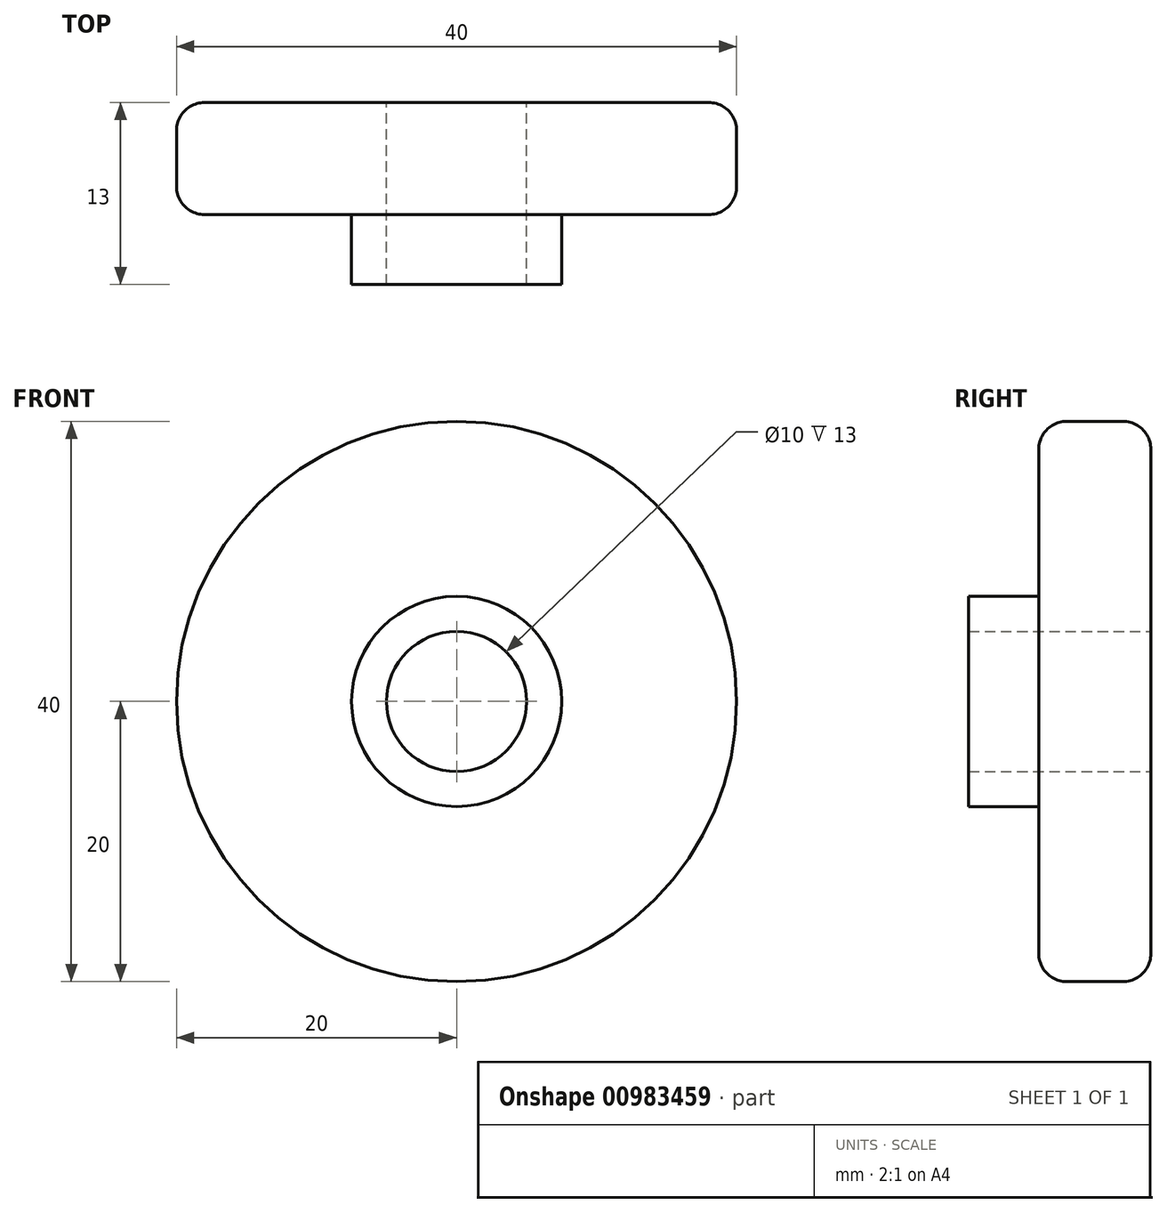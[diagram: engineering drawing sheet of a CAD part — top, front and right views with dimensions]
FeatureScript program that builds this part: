
annotation { "Feature Type Name" : "Feature", "Feature Type Description" : "" }
export const myFeature = defineFeature(function(context is Context, id is Id, definition is map)
    precondition{}
    {
        {
            var Q0;
            Q0=qCreatedBy(makeId("Front.planeOp"),FACE);
            var sketch = newSketch(context, id + "F0", { "sketchPlane" : qUnion([Q0])});
            skCircle(sketch, "E0", {"center": v(0, 0) * mm, "radius": 5 * mm});
            skCircle(sketch, "E1", {"center": v(0, 0) * mm, "radius": 20 * mm});
            skCircle(sketch, "E2", {"center": v(0, 0) * mm, "radius": 7.5 * mm});
            skSolve(sketch);
        }
        {
            var Q0;
            Q0=makeQuery(id+"F0.imprint","IMPRINT",FACE,{"disambiguationData":[TD([[makeQuery(id+"F0.imprint","IMPRINT",EDGE,{"derivedFrom":sQuery(id+"F0.wireOp",EDGE,"E1")}),1.0]])]});
            var Q1;
            Q1=makeQuery(id+"F0.imprint","IMPRINT",FACE,{"disambiguationData":[TD([[makeQuery(id+"F0.imprint","IMPRINT",EDGE,{"derivedFrom":sQuery(id+"F0.wireOp",EDGE,"E0")}),-1.0]])]});
            extrude(context, id + "F1", {"entities" : qUnion([Q0, Q1]), "depth" : 8 * mm, "offsetDistance" : 25 * mm});
        }
        {
            var Q0;
            Q0=makeQuery(id+"F0.imprint","IMPRINT",FACE,{"disambiguationData":[TD([[makeQuery(id+"F0.imprint","IMPRINT",EDGE,{"derivedFrom":sQuery(id+"F0.wireOp",EDGE,"E0")}),-1.0]])]});
            extrude(context, id + "F2", {"entities" : qUnion([Q0]), "operationType" : NewBodyOperationType.ADD, "depth" : 13 * mm, "offsetDistance" : 25 * mm});
        }
        {
            var Q0;
            Q0=makeQuery(id+"F1.opExtrude","CAP_EDGE",EDGE,{"disambiguationData":[OSD([sQuery(id+"F0.wireOp",EDGE,"E1")])],"isStart":true});
            var Q1;
            Q1=makeQuery(id+"F1.opExtrude","CAP_EDGE",EDGE,{"disambiguationData":[OSD([sQuery(id+"F0.wireOp",EDGE,"E1")])],"isStart":false});
            fillet(context, id + "F3", {"entities" : qUnion([Q0, Q1]), "radius" : 2 * mm, "tangentPropagation" : true, "allowEdgeOverflow" : false});
        }
    });
